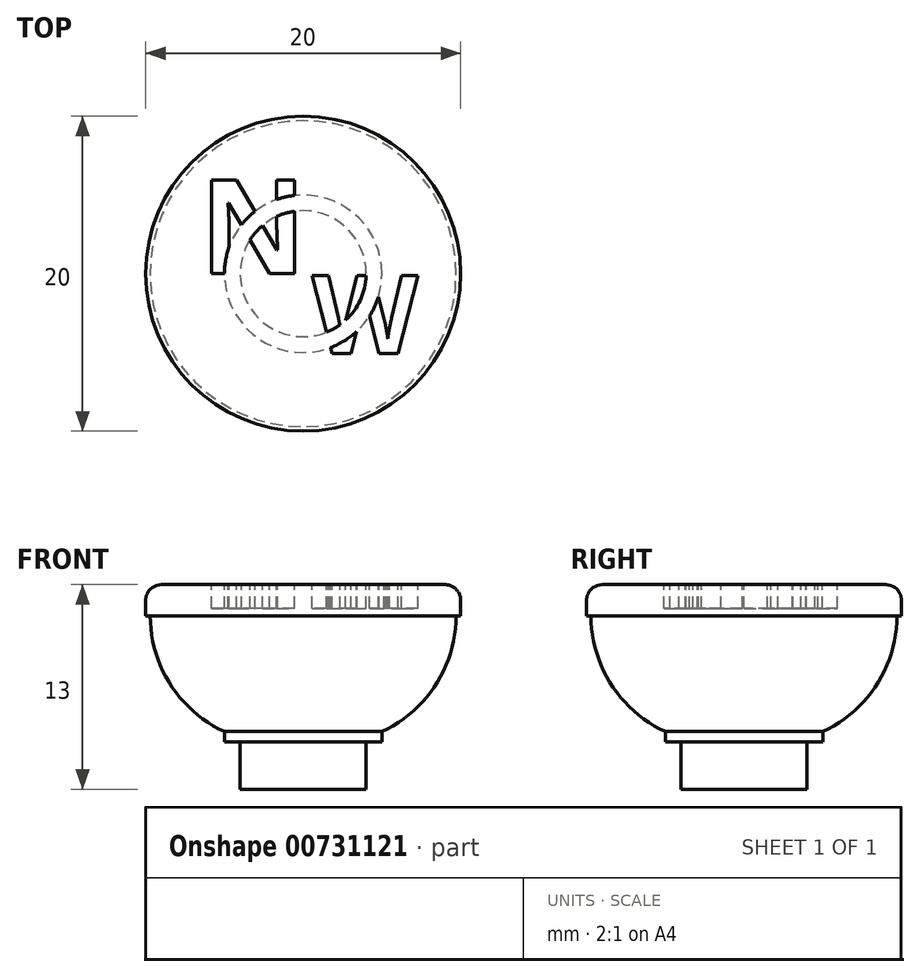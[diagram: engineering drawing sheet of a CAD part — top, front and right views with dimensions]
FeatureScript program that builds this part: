
annotation { "Feature Type Name" : "Feature", "Feature Type Description" : "" }
export const myFeature = defineFeature(function(context is Context, id is Id, definition is map)
    precondition{}
    {
        {
            var Q0;
            Q0=qCreatedBy(makeId("Top.planeOp"),FACE);
            var sketch = newSketch(context, id + "F0", { "sketchPlane" : qUnion([Q0])});
            skCircle(sketch, "E0", {"center": v(0, 0) * mm, "radius": 10 * mm});
            skCircle(sketch, "E1", {"center": v(0, 0) * mm, "radius": 4 * mm});
            skCircle(sketch, "E2", {"center": v(0, 0) * mm, "radius": 5 * mm});
            skSolve(sketch);
        }
        {
            var Q0;
            Q0=makeQuery(id+"F0.imprint","IMPRINT",FACE,{"disambiguationData":[TD([[makeQuery(id+"F0.imprint","IMPRINT",EDGE,{"derivedFrom":sQuery(id+"F0.wireOp",EDGE,"E1")}),1.0]])]});
            extrude(context, id + "F1", {"entities" : qUnion([Q0]), "oppositeDirection" : true, "depth" : 13 * mm, "offsetDistance" : 25 * mm});
        }
        {
            var Q0;
            Q0=makeQuery(id+"F0.imprint","IMPRINT",FACE,{"disambiguationData":[TD([[makeQuery(id+"F0.imprint","IMPRINT",EDGE,{"derivedFrom":sQuery(id+"F0.wireOp",EDGE,"E0")}),1.0]])]});
            var Q1;
            Q1=makeQuery(id+"F0.imprint","IMPRINT",FACE,{"disambiguationData":[TD([[makeQuery(id+"F0.imprint","IMPRINT",EDGE,{"derivedFrom":sQuery(id+"F0.wireOp",EDGE,"E1")}),-1.0]])]});
            extrude(context, id + "F2", {"entities" : qUnion([Q0, Q1]), "operationType" : NewBodyOperationType.ADD, "oppositeDirection" : true, "depth" : 2 * mm, "offsetDistance" : 25 * mm});
        }
        {
            var Q0;
            Q0=makeQuery(id+"F2.opExtrude","CAP_EDGE",EDGE,{"disambiguationData":[OSD([sQuery(id+"F0.wireOp",EDGE,"E0")])],"isStart":true});
            fillet(context, id + "F3", {"entities" : qUnion([Q0]), "radius" : 1 * mm, "tangentPropagation" : true, "allowEdgeOverflow" : false});
        }
        {
            var Q0;
            Q0=qCreatedBy(makeId("Top.planeOp"),FACE);
            var sketch = newSketch(context, id + "F4", { "sketchPlane" : qUnion([Q0])});
            skText(sketch, "E3", { "text": "N", "fontName": "OpenSans-Bold.ttf"});
            skText(sketch, "E4", { "text": "W", "fontName": "OpenSans-Bold.ttf"});
            const initialGuessF4  = {"E3": [-0.00657, 0, 1, 0, 0.006], "E4": [0.00057, -0.00507, 1, 0, 0.005]};
            skSetInitialGuess(sketch, initialGuessF4);
            skSolve(sketch);
        }
        {
            var Q0;
            Q0=makeQuery(id+"F4.imprint","IMPRINT",FACE,{"disambiguationData":[TD([[makeQuery(id+"F4.imprint","IMPRINT",EDGE,{"derivedFrom":sQuery(id+"F4.wireOp",EDGE,"E3.sketch_text.stroke-0")}),-1.0]])]});
            var Q1;
            Q1=makeQuery(id+"F4.imprint","IMPRINT",FACE,{"disambiguationData":[TD([[makeQuery(id+"F4.imprint","IMPRINT",EDGE,{"derivedFrom":sQuery(id+"F4.wireOp",EDGE,"E4.sketch_text.stroke-0")}),-1.0]])]});
            var Q2;
            Q2=makeQuery(id+"F0.imprint","IMPRINT",FACE,{"disambiguationData":[TD([[makeQuery(id+"F0.imprint","IMPRINT",EDGE,{"derivedFrom":sQuery(id+"F0.wireOp",EDGE,"E1")}),-1.0]])]});
            extrude(context, id + "F5", {"entities" : qUnion([Q0, Q1, Q2]), "operationType" : NewBodyOperationType.REMOVE, "oppositeDirection" : true, "depth" : 1.5 * mm, "offsetDistance" : 25 * mm});
        }
        {
            var Q0;
            Q0=qCreatedBy(makeId("Front.planeOp"),FACE);
            var sketch = newSketch(context, id + "F6", { "sketchPlane" : qUnion([Q0])});
            skLineSegment(sketch, "E5", {"start": v(0, 0) * mm, "end": v(0, -9.93) * mm});
            skLineSegment(sketch, "E6", {"start": v(0, -1.56) * mm, "end": v(9.7, -1.56) * mm});
            skArc(sketch, "E7", {"start": v(0, -9.93) * mm, "mid": v(6.9, -8.11) * mm, "end": v(9.7, -1.56) * mm});
            skSolve(sketch);
        }
        {
            var Q0;
            Q0=makeQuery(id+"F0.imprint","IMPRINT",FACE,{"disambiguationData":[TD([[makeQuery(id+"F0.imprint","IMPRINT",EDGE,{"derivedFrom":sQuery(id+"F0.wireOp",EDGE,"E1")}),-1.0]])]});
            extrude(context, id + "F7", {"entities" : qUnion([Q0]), "operationType" : NewBodyOperationType.ADD, "oppositeDirection" : true, "depth" : 10 * mm, "offsetDistance" : 25 * mm});
        }
        {
            var Q0;
            {var subQ2=sQuery(id+"F6.wireOp",EDGE,"E6");Q0=makeQuery(id+"F6.imprint","IMPRINT",FACE,{"disambiguationData":[TD([[makeQuery(id+"F6.imprint","IMPRINT",EDGE,{"derivedFrom":subQ2}),-1.0]])]});}
            var Q1;
            Q1=sQuery(id+"F6.wireOp",EDGE,"E5");
            revolve(context, id + "F8", {"operationType" : NewBodyOperationType.ADD, "surfaceOperationType" : NewSurfaceOperationType.NEW, "entities" : qUnion([Q0]), "axis" : qUnion([Q1]), "revolveType" : RevolveType.FULL});
        }
    });
